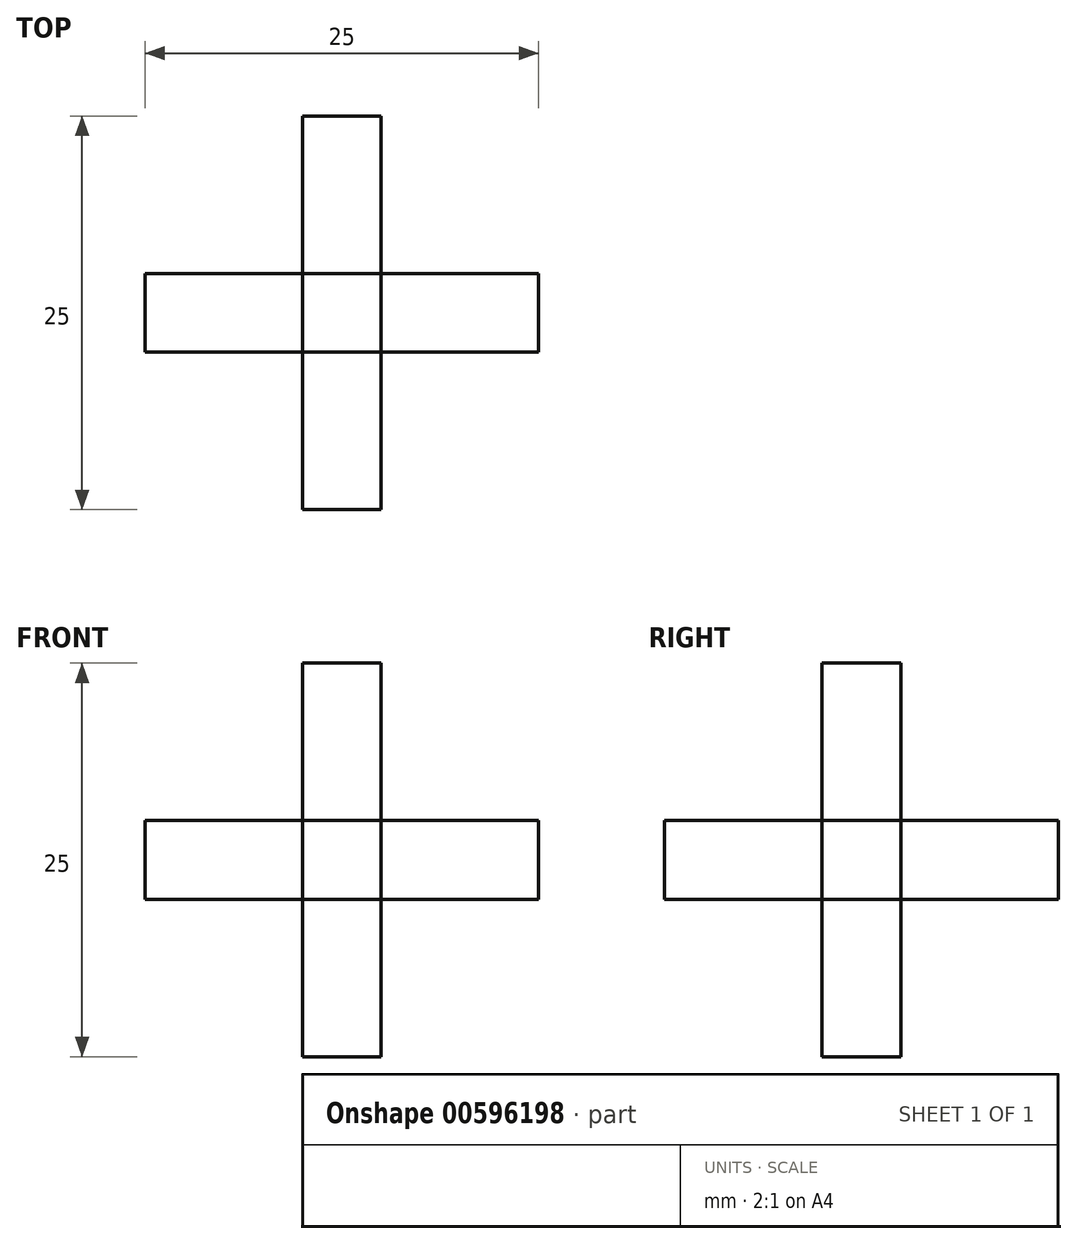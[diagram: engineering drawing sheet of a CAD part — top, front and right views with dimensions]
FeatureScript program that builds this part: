
annotation { "Feature Type Name" : "Feature", "Feature Type Description" : "" }
export const myFeature = defineFeature(function(context is Context, id is Id, definition is map)
    precondition{}
    {
        {
            var Q0;
            Q0=qCreatedBy(makeId("Top.planeOp"),FACE);
            var sketch = newSketch(context, id + "F0", { "sketchPlane" : qUnion([Q0])});
            skLineSegment(sketch, "E0.bottom", {"start": v(12.5, 2.5) * mm, "end": v(2.5, 2.5) * mm});
            skLineSegment(sketch, "E0.top", {"start": v(12.5, -2.5) * mm, "end": v(2.5, -2.5) * mm});
            skLineSegment(sketch, "E0.left", {"start": v(12.5, 2.5) * mm, "end": v(12.5, -2.5) * mm});
            skLineSegment(sketch, "E0.right", {"start": v(-12.5, 2.5) * mm, "end": v(-12.5, -2.5) * mm});
            skPoint(sketch, "E0.middle", {"position": v(0, 0) * mm});
            skLineSegment(sketch, "E1.bottom", {"start": v(2.5, 12.5) * mm, "end": v(-2.5, 12.5) * mm});
            skLineSegment(sketch, "E1.top", {"start": v(2.5, -12.5) * mm, "end": v(-2.5, -12.5) * mm});
            skLineSegment(sketch, "E1.left", {"start": v(2.5, 12.5) * mm, "end": v(2.5, 2.5) * mm});
            skLineSegment(sketch, "E1.right", {"start": v(-2.5, 12.5) * mm, "end": v(-2.5, 2.5) * mm});
            skLineSegment(sketch, "E2.trimOffspring", {"start": v(-2.5, -2.5) * mm, "end": v(-2.5, -12.5) * mm});
            skLineSegment(sketch, "E3.trimOffspring", {"start": v(-2.5, 2.5) * mm, "end": v(-12.5, 2.5) * mm});
            skLineSegment(sketch, "E4.trimOffspring", {"start": v(2.5, -2.5) * mm, "end": v(2.5, -12.5) * mm});
            skLineSegment(sketch, "E5.trimOffspring", {"start": v(-2.5, -2.5) * mm, "end": v(-12.5, -2.5) * mm});
            skSolve(sketch);
        }
        {
            var Q0;
            Q0 = qSketchRegion(id + "F0", true);
            extrude(context, id + "F1", {"entities" : qUnion([Q0]), "endBound" : BoundingType.SYMMETRIC, "depth" : 5 * mm, "offsetDistance" : 25 * mm});
        }
        {
            var Q0;
            Q0=qCreatedBy(makeId("Top.planeOp"),FACE);
            var sketch = newSketch(context, id + "F2", { "sketchPlane" : qUnion([Q0])});
            skLineSegment(sketch, "E6.bottom", {"start": v(2.5, 2.5) * mm, "end": v(-2.5, 2.5) * mm});
            skLineSegment(sketch, "E6.top", {"start": v(2.5, -2.5) * mm, "end": v(-2.5, -2.5) * mm});
            skLineSegment(sketch, "E6.left", {"start": v(2.5, 2.5) * mm, "end": v(2.5, -2.5) * mm});
            skLineSegment(sketch, "E6.right", {"start": v(-2.5, 2.5) * mm, "end": v(-2.5, -2.5) * mm});
            skPoint(sketch, "E6.middle", {"position": v(0, 0) * mm});
            skSolve(sketch);
        }
        {
            var Q0;
            Q0 = qSketchRegion(id + "F2", true);
            extrude(context, id + "F3", {"entities" : qUnion([Q0]), "operationType" : NewBodyOperationType.ADD, "endBound" : BoundingType.SYMMETRIC, "depth" : 25 * mm, "offsetDistance" : 25 * mm});
        }
    });
